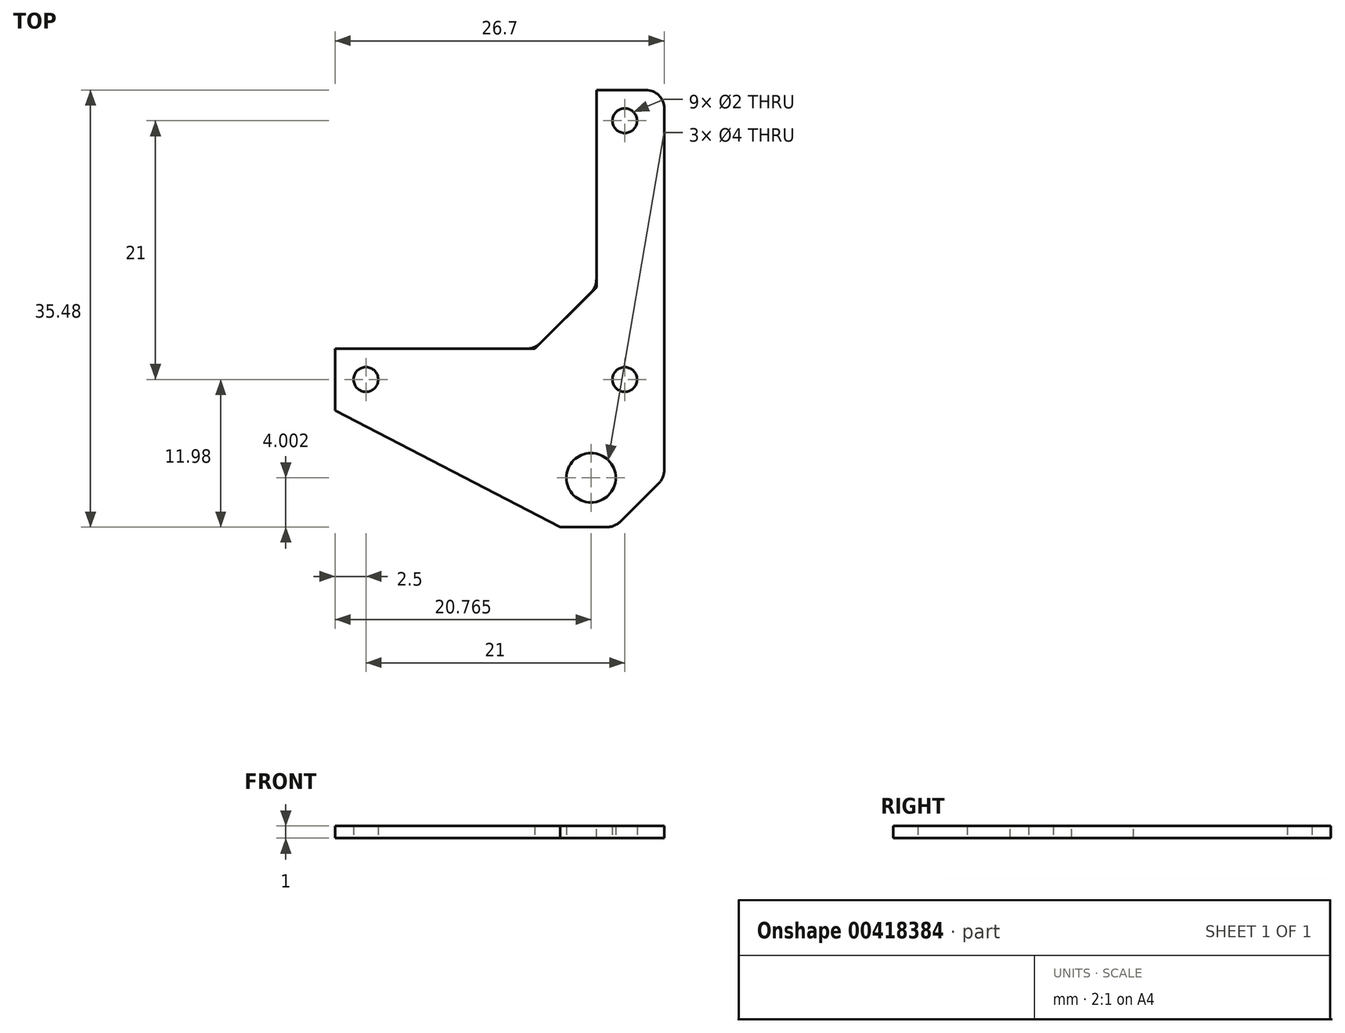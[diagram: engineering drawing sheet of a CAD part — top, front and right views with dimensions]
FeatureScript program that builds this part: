
annotation { "Feature Type Name" : "Feature", "Feature Type Description" : "" }
export const myFeature = defineFeature(function(context is Context, id is Id, definition is map)
    precondition{}
    {
        {
            var Q0;
            Q0=qCreatedBy(makeId("Top.planeOp"),FACE);
            var sketch = newSketch(context, id + "F0", { "sketchPlane" : qUnion([Q0])});
            skArc(sketch, "E0", {"start": v(-6.25, 0) * mm, "mid": v(0, -6.25) * mm, "end": v(6.25, 0) * mm});
            skCircle(sketch, "E1", {"center": v(10.5, 0) * mm, "radius": 1 * mm});
            skCircle(sketch, "E2", {"center": v(10.5, -21) * mm, "radius": 1 * mm});
            skCircle(sketch, "E3.MirrorC", {"center": v(-10.5, 0) * mm, "radius": 1 * mm});
            skCircle(sketch, "E4.MirrorC", {"center": v(-10.5, -21) * mm, "radius": 1 * mm});
            skLineSegment(sketch, "E5.bottom", {"start": v(-10.5, 0) * mm, "end": v(10.5, 0) * mm, "construction": true});
            skLineSegment(sketch, "E5.top", {"start": v(-10.5, -21) * mm, "end": v(10.5, -21) * mm, "construction": true});
            skLineSegment(sketch, "E5.left", {"start": v(-10.5, 0) * mm, "end": v(-10.5, -21) * mm, "construction": true});
            skLineSegment(sketch, "E5.right", {"start": v(10.5, 0) * mm, "end": v(10.5, -21) * mm, "construction": true});
            skLineSegment(sketch, "E6", {"start": v(0, 0) * mm, "end": v(7.76, -28.98) * mm, "construction": true});
            skCircle(sketch, "E7", {"center": v(7.76, -28.98) * mm, "radius": 2 * mm});
            skLineSegment(sketch, "E8.bottom", {"start": v(-13, 2.5) * mm, "end": v(-6.25, 2.5) * mm});
            skLineSegment(sketch, "E8.top", {"start": v(-13, -32.98) * mm, "end": v(13.7, -32.98) * mm});
            skLineSegment(sketch, "E8.left", {"start": v(-13, 2.5) * mm, "end": v(-13, -32.98) * mm});
            skLineSegment(sketch, "E8.right", {"start": v(13.7, 2.5) * mm, "end": v(13.7, -32.98) * mm});
            skLineSegment(sketch, "E9", {"start": v(6.25, 0) * mm, "end": v(6.25, 2.5) * mm});
            skLineSegment(sketch, "E10", {"start": v(-6.25, 0) * mm, "end": v(-6.25, 2.5) * mm});
            skLineSegment(sketch, "E11.trimOffspring", {"start": v(6.25, 2.5) * mm, "end": v(13.7, 2.5) * mm});
            skArc(sketch, "E12", {"start": v(-13, -4.77) * mm, "mid": v(-16.75, -10.5) * mm, "end": v(-13, -16.23) * mm});
            skPoint(sketch, "E12.centerSnap0", {"position": v(-10.5, -10.5) * mm});
            skLineSegment(sketch, "E13", {"start": v(-6.25, 2.5) * mm, "end": v(6.25, 2.5) * mm});
            skLineSegment(sketch, "E14", {"start": v(-10.5, -4.25) * mm, "end": v(-13, -4.25) * mm});
            skLineSegment(sketch, "E15", {"start": v(-10.5, -16.75) * mm, "end": v(-13, -16.75) * mm});
            skArc(sketch, "E16.trimOffspring", {"start": v(-10.5, -16.75) * mm, "mid": v(-4.25, -10.5) * mm, "end": v(-10.5, -4.25) * mm});
            skSolve(sketch);
        }
        {
            var Q0;
            Q0=makeQuery(id+"F0.imprint","IMPRINT",FACE,{"disambiguationData":[TD([[makeQuery(id+"F0.imprint","IMPRINT",EDGE,{"derivedFrom":sQuery(id+"F0.wireOp",EDGE,"E0")}),1.0]])]});
            var Q1;
            Q1=makeQuery(id+"F0.imprint","IMPRINT",FACE,{"disambiguationData":[TD([[makeQuery(id+"F0.imprint","IMPRINT",EDGE,{"derivedFrom":sQuery(id+"F0.wireOp",EDGE,"E0")}),-1.0]])]});
            extrude(context, id + "F1", {"entities" : qUnion([Q0, Q1]), "depth" : 1 * mm});
        }
        {
            var Q0;
            Q0=makeQuery(id+"F1.opExtrude","CAP_FACE",FACE,{"disambiguationData":[OSD([sQuery(id+"F0.wireOp",EDGE,"E0"),sQuery(id+"F0.wireOp",EDGE,"E1"),sQuery(id+"F0.wireOp",EDGE,"E2"),sQuery(id+"F0.wireOp",EDGE,"E3.MirrorC"),sQuery(id+"F0.wireOp",EDGE,"E4.MirrorC"),sQuery(id+"F0.wireOp",EDGE,"E7"),sQuery(id+"F0.wireOp",EDGE,"E8.bottom"),sQuery(id+"F0.wireOp",EDGE,"E8.top"),sQuery(id+"F0.wireOp",EDGE,"E8.left"),sQuery(id+"F0.wireOp",EDGE,"E8.right"),sQuery(id+"F0.wireOp",EDGE,"E9"),sQuery(id+"F0.wireOp",EDGE,"E10"),sQuery(id+"F0.wireOp",EDGE,"E11.trimOffspring")])],"isStart":false});
            var sketch = newSketch(context, id + "F2", { "sketchPlane" : qUnion([Q0])});
            skLineSegment(sketch, "E17", {"start": v(-13, -23.5) * mm, "end": v(5.26, -32.98) * mm});
            skLineSegment(sketch, "E18", {"start": v(5.26, -32.98) * mm, "end": v(-13, -32.98) * mm});
            skLineSegment(sketch, "E19", {"start": v(-13, -32.98) * mm, "end": v(-13, -23.5) * mm});
            skCircle(sketch, "E20.0", {"center": v(-10.5, -21) * mm, "radius": 1 * mm, "construction": true});
            skCircle(sketch, "E21.0", {"center": v(7.76, -28.98) * mm, "radius": 2 * mm, "construction": true});
            skLineSegment(sketch, "E22", {"start": v(-13, -18.5) * mm, "end": v(13.7, -18.5) * mm});
            skLineSegment(sketch, "E23", {"start": v(8.2, 2.5) * mm, "end": v(8.2, -18.5) * mm});
            skSolve(sketch);
        }
        {
            var Q0;
            Q0 = qSketchRegion(id + "F2", true);
            var Q1;
            {var subQ4=sQuery(id+"F2.wireOp",EDGE,"E23");Q1=makeQuery(id+"F2.imprint","IMPRINT",FACE,{"disambiguationData":[TD([[makeQuery(id+"F2.imprint","IMPRINT",EDGE,{"derivedFrom":subQ4}),-1.0]])]});}
            extrude(context, id + "F3", {"entities" : qUnion([Q0, Q1]), "operationType" : NewBodyOperationType.REMOVE, "endBound" : BoundingType.UP_TO_NEXT, "oppositeDirection" : true, "depth" : 25 * mm});
        }
        {
            var Q0;
            Q0=makeQuery(id+"F1.opExtrude","SWEPT_EDGE",EDGE,{"disambiguationData":[OSD([sQuery(id+"F0.wireOp",EDGE,"E8.top"),sQuery(id+"F0.wireOp",EDGE,"E8.right")])]});
            chamfer(context, id + "F4", {"entities" : qUnion([Q0]), "width" : 4 * mm, "tangentPropagation" : true});
        }
        {
            var Q0;
            Q0=makeQuery(id+"F3.boolean.opBoolean","COPY",EDGE,{"derivedFrom":makeQuery(id+"F3.opExtrude","SWEPT_EDGE",EDGE,{"disambiguationData":[OSD([sQuery(id+"F2.wireOp",EDGE,"E22"),sQuery(id+"F2.wireOp",EDGE,"E23")])]})});
            chamfer(context, id + "F5", {"entities" : qUnion([Q0]), "width" : 5 * mm, "tangentPropagation" : true});
        }
        {
            var Q0;
            Q0=makeQuery(id+"F3.boolean.opBoolean","COPY",EDGE,{"derivedFrom":makeQuery(id+"F3.opExtrude","SWEPT_EDGE",EDGE,{"disambiguationData":[OSD([sQuery(id+"F0.wireOp",EDGE,"E8.left"),sQuery(id+"F2.wireOp",EDGE,"E17"),sQuery(id+"F2.wireOp",EDGE,"E19")])]})});
            var Q1;
            Q1=makeQuery(id+"F3.boolean.opBoolean","COPY",EDGE,{"derivedFrom":makeQuery(id+"F3.opExtrude","SWEPT_EDGE",EDGE,{"disambiguationData":[OSD([sQuery(id+"F0.wireOp",EDGE,"E8.top"),sQuery(id+"F2.wireOp",EDGE,"E17"),sQuery(id+"F2.wireOp",EDGE,"E18")])]})});
            var Q2;
            {var subQ0=sQuery(id+"F0.wireOp",EDGE,"E8.top");Q2=makeQuery(id+"F4.opChamfer","BLEND_EDGE",EDGE,{"blendedFrom":[makeQuery(id+"F1.opExtrude","SWEPT_EDGE",EDGE,{"disambiguationData":[OSD([subQ0,sQuery(id+"F0.wireOp",EDGE,"E8.right")])]}),makeQuery(id+"F1.opExtrude","SWEPT_FACE",FACE,{"disambiguationData":[OSD([subQ0])]})],"blendedInto":[makeQuery(id+"F1.opExtrude","SWEPT_FACE",FACE,{"disambiguationData":[OSD([subQ0])]})]});}
            var Q3;
            {var subQ0=sQuery(id+"F0.wireOp",EDGE,"E8.right");Q3=makeQuery(id+"F4.opChamfer","BLEND_EDGE",EDGE,{"blendedFrom":[makeQuery(id+"F1.opExtrude","SWEPT_EDGE",EDGE,{"disambiguationData":[OSD([sQuery(id+"F0.wireOp",EDGE,"E8.top"),subQ0])]}),makeQuery(id+"F1.opExtrude","SWEPT_FACE",FACE,{"disambiguationData":[OSD([subQ0])]})],"blendedInto":[makeQuery(id+"F1.opExtrude","SWEPT_FACE",FACE,{"disambiguationData":[OSD([subQ0])]})]});}
            var Q4;
            {var subQ0=sQuery(id+"F2.wireOp",EDGE,"E23");Q4=makeQuery(id+"F5.opChamfer","BLEND_EDGE",EDGE,{"blendedFrom":[makeQuery(id+"F3.boolean.opBoolean","COPY",EDGE,{"derivedFrom":makeQuery(id+"F3.opExtrude","SWEPT_EDGE",EDGE,{"disambiguationData":[OSD([sQuery(id+"F2.wireOp",EDGE,"E22"),subQ0])]})}),makeQuery(id+"F3.boolean.opBoolean","COPY",FACE,{"derivedFrom":makeQuery(id+"F3.opExtrude","SWEPT_FACE",FACE,{"disambiguationData":[OSD([subQ0])]})})],"blendedInto":[makeQuery(id+"F3.boolean.opBoolean","COPY",FACE,{"derivedFrom":makeQuery(id+"F3.opExtrude","SWEPT_FACE",FACE,{"disambiguationData":[OSD([subQ0])]})})]});}
            var Q5;
            {var subQ0=sQuery(id+"F2.wireOp",EDGE,"E22");Q5=makeQuery(id+"F5.opChamfer","BLEND_EDGE",EDGE,{"blendedFrom":[makeQuery(id+"F3.boolean.opBoolean","COPY",EDGE,{"derivedFrom":makeQuery(id+"F3.opExtrude","SWEPT_EDGE",EDGE,{"disambiguationData":[OSD([subQ0,sQuery(id+"F2.wireOp",EDGE,"E23")])]})}),makeQuery(id+"F3.boolean.opBoolean","COPY",FACE,{"derivedFrom":makeQuery(id+"F3.opExtrude","SWEPT_FACE",FACE,{"disambiguationData":[OSD([subQ0])]})})],"blendedInto":[makeQuery(id+"F3.boolean.opBoolean","COPY",FACE,{"derivedFrom":makeQuery(id+"F3.opExtrude","SWEPT_FACE",FACE,{"disambiguationData":[OSD([subQ0])]})})]});}
            var Q6;
            Q6=makeQuery(id+"F3.boolean.opBoolean","COPY",EDGE,{"derivedFrom":makeQuery(id+"F3.opExtrude","SWEPT_EDGE",EDGE,{"disambiguationData":[OSD([sQuery(id+"F0.wireOp",EDGE,"E8.left"),sQuery(id+"F2.wireOp",EDGE,"E22")])]})});
            var Q7;
            Q7=makeQuery(id+"F1.opExtrude","SWEPT_EDGE",EDGE,{"disambiguationData":[OSD([sQuery(id+"F0.wireOp",EDGE,"E8.right"),sQuery(id+"F0.wireOp",EDGE,"E11.trimOffspring")])]});
            var Q8;
            Q8=makeQuery(id+"F3.boolean.opBoolean","COPY",EDGE,{"derivedFrom":makeQuery(id+"F3.opExtrude","SWEPT_EDGE",EDGE,{"disambiguationData":[OSD([sQuery(id+"F0.wireOp",EDGE,"E8.bottom"),sQuery(id+"F0.wireOp",EDGE,"E11.trimOffspring"),sQuery(id+"F0.wireOp",EDGE,"E13"),sQuery(id+"F2.wireOp",EDGE,"E23")])]})});
            fillet(context, id + "F6", {"entities" : qUnion([Q0, Q1, Q2, Q3, Q4, Q5, Q6, Q7, Q8]), "radius" : 1.5 * mm, "tangentPropagation" : true, "allowEdgeOverflow" : false});
        }
    });
